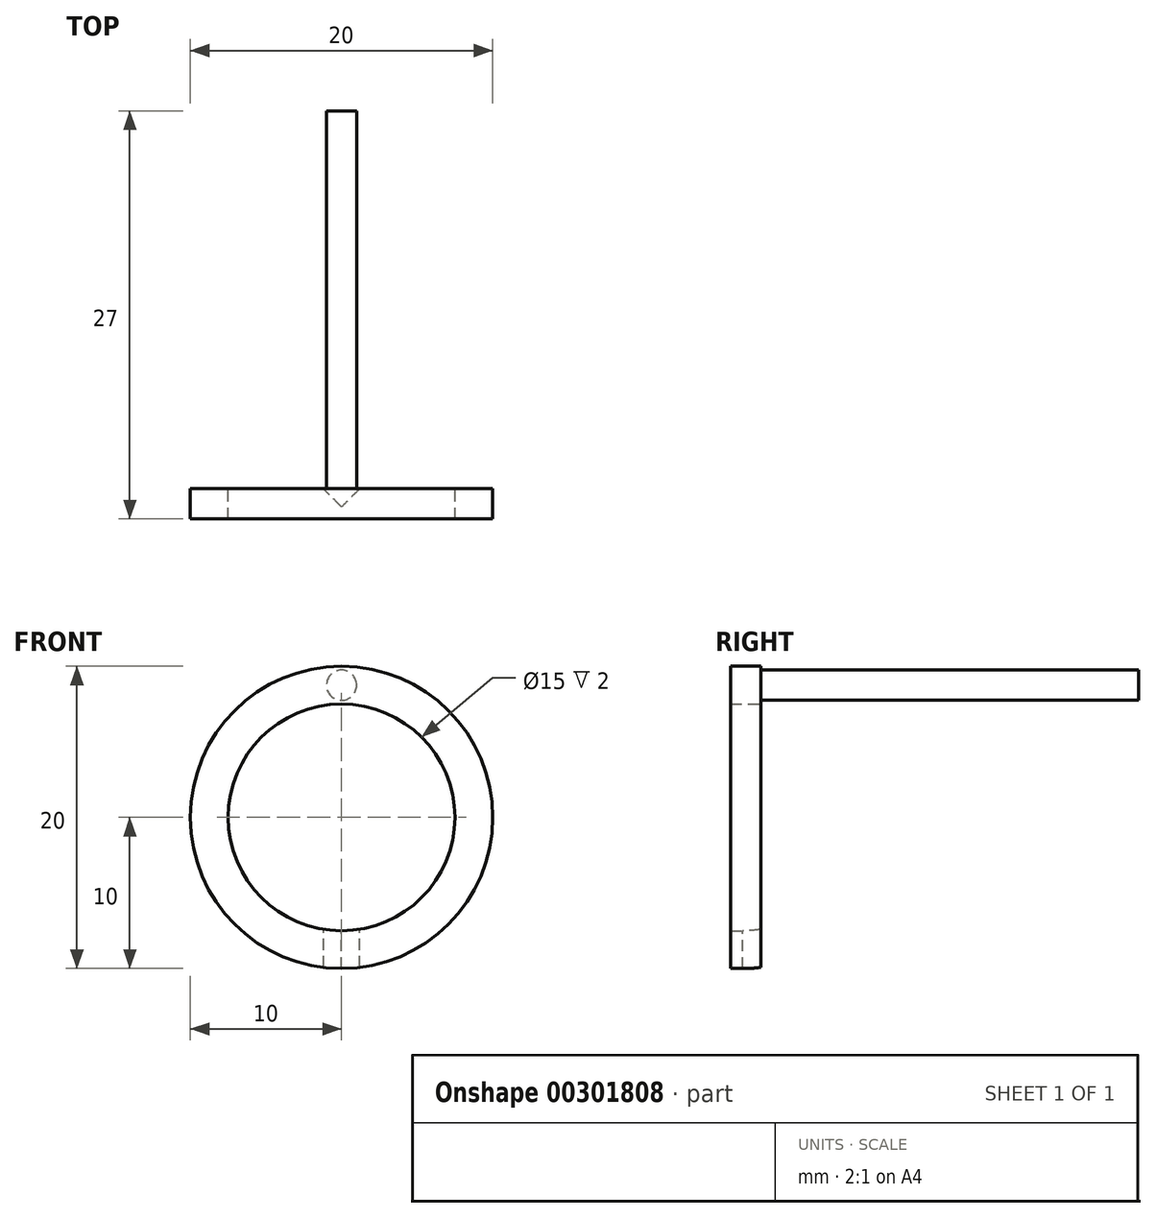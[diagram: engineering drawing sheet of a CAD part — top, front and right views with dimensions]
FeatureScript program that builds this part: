
annotation { "Feature Type Name" : "Feature", "Feature Type Description" : "" }
export const myFeature = defineFeature(function(context is Context, id is Id, definition is map)
    precondition{}
    {
        {
            var Q0;
            Q0=qCreatedBy(makeId("Front.planeOp"),FACE);
            var sketch = newSketch(context, id + "F0", { "sketchPlane" : qUnion([Q0])});
            skCircle(sketch, "E0", {"center": v(0, 0) * mm, "radius": 10 * mm});
            skCircle(sketch, "E1", {"center": v(0, 0) * mm, "radius": 7.5 * mm});
            skSolve(sketch);
        }
        {
            var Q0;
            Q0 = qSketchRegion(id + "F0", true);
            extrude(context, id + "F1", {"entities" : qUnion([Q0]), "depth" : 2 * mm});
        }
        {
            var Q0;
            Q0=qCreatedBy(makeId("Top.planeOp"),FACE);
            var sketch = newSketch(context, id + "F2", { "sketchPlane" : qUnion([Q0])});
            skLineSegment(sketch, "E2", {"start": v(0, 0) * mm, "end": v(0, -1.2) * mm, "construction": true});
            skLineSegment(sketch, "E3", {"start": v(0, -1.2) * mm, "end": v(-1.2, 0) * mm});
            skLineSegment(sketch, "E4", {"start": v(-1.2, 0) * mm, "end": v(1.2, 0) * mm});
            skLineSegment(sketch, "E5", {"start": v(1.2, 0) * mm, "end": v(0, -1.2) * mm});
            skSolve(sketch);
        }
        {
            var Q0;
            Q0=makeQuery(id+"F2.imprint","IMPRINT",FACE,{"disambiguationData":[TD([[makeQuery(id+"F2.imprint","IMPRINT",EDGE,{"derivedFrom":sQuery(id+"F2.wireOp",EDGE,"E3")}),-1.0]])]});
            var Q1;
            Q1=sQuery(id+"F2.wireOp",EDGE,"E2");
            extrude(context, id + "F3", {"entities" : qUnion([Q0]), "operationType" : NewBodyOperationType.REMOVE, "surfaceEntities" : qUnion([Q1]), "oppositeDirection" : true, "depth" : 25 * mm});
        }
        {
            var Q0;
            Q0=qCreatedBy(makeId("Front.planeOp"),FACE);
            var sketch = newSketch(context, id + "F4", { "sketchPlane" : qUnion([Q0])});
            skLineSegment(sketch, "E6", {"start": v(0, 0) * mm, "end": v(0, 8.75) * mm, "construction": true});
            skCircle(sketch, "E7", {"center": v(0, 8.75) * mm, "radius": 1 * mm});
            skSolve(sketch);
        }
        {
            var Q0;
            Q0 = qSketchRegion(id + "F4", true);
            extrude(context, id + "F5", {"entities" : qUnion([Q0]), "operationType" : NewBodyOperationType.ADD, "oppositeDirection" : true, "depth" : 25 * mm});
        }
    });
